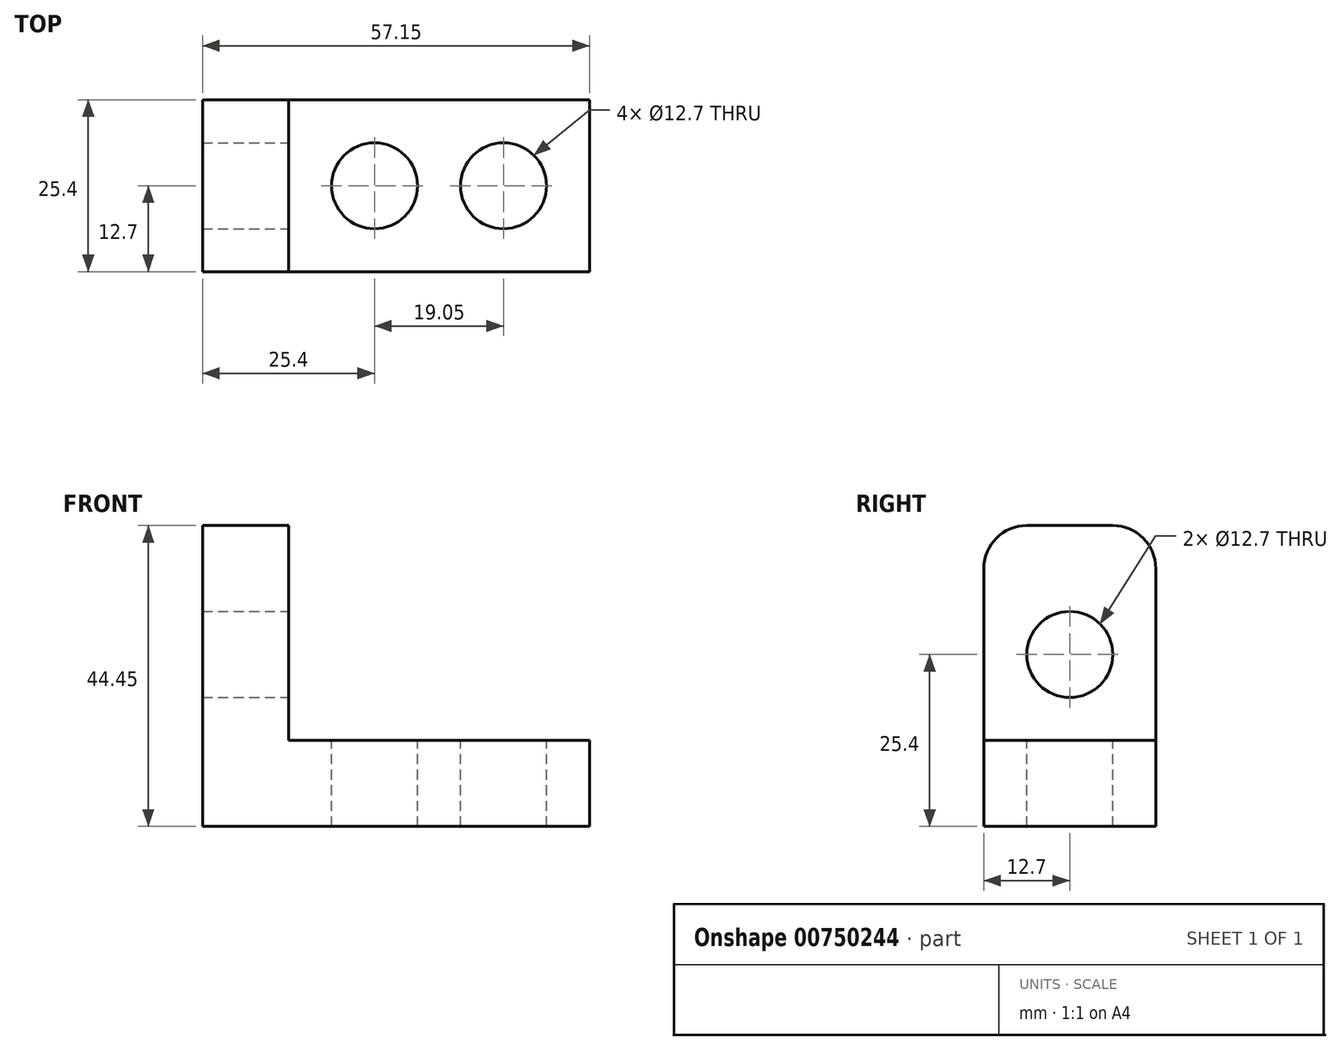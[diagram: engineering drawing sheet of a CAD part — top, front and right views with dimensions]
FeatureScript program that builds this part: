
annotation { "Feature Type Name" : "Feature", "Feature Type Description" : "" }
export const myFeature = defineFeature(function(context is Context, id is Id, definition is map)
    precondition{}
    {
        {
            var Q0;
            Q0=qCreatedBy(makeId("Front.planeOp"),FACE);
            var sketch = newSketch(context, id + "F0", { "sketchPlane" : qUnion([Q0])});
            skLineSegment(sketch, "E0", {"start": v(0, 0) * mm, "end": v(57.15, 0) * mm});
            skLineSegment(sketch, "E1", {"start": v(57.15, 0) * mm, "end": v(57.15, 44.45) * mm});
            skLineSegment(sketch, "E2", {"start": v(57.15, 44.45) * mm, "end": v(0, 44.45) * mm});
            skLineSegment(sketch, "E3", {"start": v(0, 44.45) * mm, "end": v(0, 0) * mm});
            skSolve(sketch);
        }
        {
            var Q0;
            Q0=makeQuery(id+"F0.imprint","IMPRINT",FACE,{"disambiguationData":[TD([[makeQuery(id+"F0.imprint","IMPRINT",EDGE,{"derivedFrom":sQuery(id+"F0.wireOp",EDGE,"E0")}),1.0]])]});
            extrude(context, id + "F1", {"entities" : qUnion([Q0]), "depth" : 25.4 * mm, "offsetDistance" : 25.4 * mm});
        }
        {
            var Q0;
            Q0=makeQuery(id+"F1.opExtrude","CAP_FACE",FACE,{"disambiguationData":[OSD([sQuery(id+"F0.wireOp",EDGE,"E0"),sQuery(id+"F0.wireOp",EDGE,"E1"),sQuery(id+"F0.wireOp",EDGE,"E2"),sQuery(id+"F0.wireOp",EDGE,"E3")])],"isStart":false});
            var sketch = newSketch(context, id + "F2", { "sketchPlane" : qUnion([Q0])});
            skLineSegment(sketch, "E4", {"start": v(12.7, 44.45) * mm, "end": v(12.7, 12.7) * mm});
            skLineSegment(sketch, "E5", {"start": v(12.7, 12.7) * mm, "end": v(57.15, 12.7) * mm});
            skLineSegment(sketch, "E6", {"start": v(57.15, 12.7) * mm, "end": v(57.15, 44.45) * mm});
            skLineSegment(sketch, "E7", {"start": v(57.15, 44.45) * mm, "end": v(12.7, 44.45) * mm});
            skSolve(sketch);
        }
        {
            var Q0;
            Q0=makeQuery(id+"F2.imprint","IMPRINT",FACE,{"disambiguationData":[TD([[makeQuery(id+"F2.imprint","IMPRINT",EDGE,{"derivedFrom":sQuery(id+"F2.wireOp",EDGE,"E4")}),1.0]])]});
            extrude(context, id + "F3", {"entities" : qUnion([Q0]), "operationType" : NewBodyOperationType.REMOVE, "oppositeDirection" : true, "depth" : 25.4 * mm, "offsetDistance" : 25.4 * mm});
        }
        {
            var Q0;
            Q0=makeQuery(id+"F3.boolean.opBoolean","COPY",FACE,{"derivedFrom":makeQuery(id+"F3.opExtrude","SWEPT_FACE",FACE,{"disambiguationData":[OSD([sQuery(id+"F2.wireOp",EDGE,"E4")])]})});
            var sketch = newSketch(context, id + "F4", { "sketchPlane" : qUnion([Q0])});
            skCircle(sketch, "E8", {"center": v(-12.7, 25.4) * mm, "radius": 6.35 * mm});
            skLineSegment(sketch, "E9", {"start": v(-12.7, 25.4) * mm, "end": v(-19.05, 25.4) * mm});
            skLineSegment(sketch, "E10", {"start": v(-19.05, 25.4) * mm, "end": v(-19.05, 44.45) * mm});
            skLineSegment(sketch, "E11", {"start": v(-19.05, 44.45) * mm, "end": v(-19.05, 25.4) * mm});
            skLineSegment(sketch, "E12", {"start": v(-12.7, 25.4) * mm, "end": v(-6.35, 25.4) * mm});
            skLineSegment(sketch, "E13", {"start": v(-6.35, 25.4) * mm, "end": v(-6.35, 44.45) * mm});
            skLineSegment(sketch, "E14", {"start": v(-6.35, 44.45) * mm, "end": v(-19.05, 44.45) * mm});
            skArc(sketch, "E15", {"start": v(-19.05, 44.45) * mm, "mid": v(-23.54, 42.6) * mm, "end": v(-25.4, 38.1) * mm});
            skArc(sketch, "E16", {"start": v(0, 38.1) * mm, "mid": v(-1.86, 42.6) * mm, "end": v(-6.35, 44.45) * mm});
            skSolve(sketch);
        }
        {
            var Q0;
            {var subQ0=sQuery(id+"F4.wireOp",EDGE,"E15");Q0=makeQuery(id+"F4.imprint","IMPRINT",FACE,{"disambiguationData":[TD([[makeQuery(id+"F4.imprint","IMPRINT",EDGE,{"derivedFrom":subQ0}),-1.0]])]});}
            var Q1;
            {var subQ0=sQuery(id+"F4.wireOp",EDGE,"E11");Q1=makeQuery(id+"F4.imprint","IMPRINT",FACE,{"disambiguationData":[TD([[makeQuery(id+"F4.imprint","IMPRINT",EDGE,{"derivedFrom":subQ0}),1.0]])]});}
            var Q2;
            {var subQ0=sQuery(id+"F4.wireOp",EDGE,"E9");Q2=makeQuery(id+"F4.imprint","IMPRINT",FACE,{"disambiguationData":[TD([[makeQuery(id+"F4.imprint","IMPRINT",EDGE,{"derivedFrom":subQ0}),-1.0]])]});}
            var Q3;
            {var subQ0=sQuery(id+"F4.wireOp",EDGE,"E9");Q3=makeQuery(id+"F4.imprint","IMPRINT",FACE,{"disambiguationData":[TD([[makeQuery(id+"F4.imprint","IMPRINT",EDGE,{"derivedFrom":subQ0}),1.0]])]});}
            var Q4;
            {var subQ0=sQuery(id+"F4.wireOp",EDGE,"E16");Q4=makeQuery(id+"F4.imprint","IMPRINT",FACE,{"disambiguationData":[TD([[makeQuery(id+"F4.imprint","IMPRINT",EDGE,{"derivedFrom":subQ0}),-1.0]])]});}
            extrude(context, id + "F5", {"entities" : qUnion([Q0, Q1, Q2, Q3, Q4]), "operationType" : NewBodyOperationType.REMOVE, "oppositeDirection" : true, "depth" : 25.4 * mm, "offsetDistance" : 25.4 * mm});
        }
        {
            var Q0;
            Q0=makeQuery(id+"F3.boolean.opBoolean","COPY",FACE,{"derivedFrom":makeQuery(id+"F3.opExtrude","SWEPT_FACE",FACE,{"disambiguationData":[OSD([sQuery(id+"F2.wireOp",EDGE,"E5")])]})});
            var sketch = newSketch(context, id + "F6", { "sketchPlane" : qUnion([Q0])});
            skCircle(sketch, "E17", {"center": v(25.4, -12.7) * mm, "radius": 6.35 * mm});
            skCircle(sketch, "E18", {"center": v(44.45, -12.7) * mm, "radius": 6.35 * mm});
            skSolve(sketch);
        }
        {
            var Q0;
            Q0=makeQuery(id+"F6.imprint","IMPRINT",FACE,{"disambiguationData":[TD([[makeQuery(id+"F6.imprint","IMPRINT",EDGE,{"derivedFrom":sQuery(id+"F6.wireOp",EDGE,"E17")}),1.0]])]});
            var Q1;
            Q1=makeQuery(id+"F6.imprint","IMPRINT",FACE,{"disambiguationData":[TD([[makeQuery(id+"F6.imprint","IMPRINT",EDGE,{"derivedFrom":sQuery(id+"F6.wireOp",EDGE,"E18")}),1.0]])]});
            extrude(context, id + "F7", {"entities" : qUnion([Q0, Q1]), "operationType" : NewBodyOperationType.REMOVE, "oppositeDirection" : true, "depth" : 25.4 * mm, "offsetDistance" : 25.4 * mm});
        }
    });
